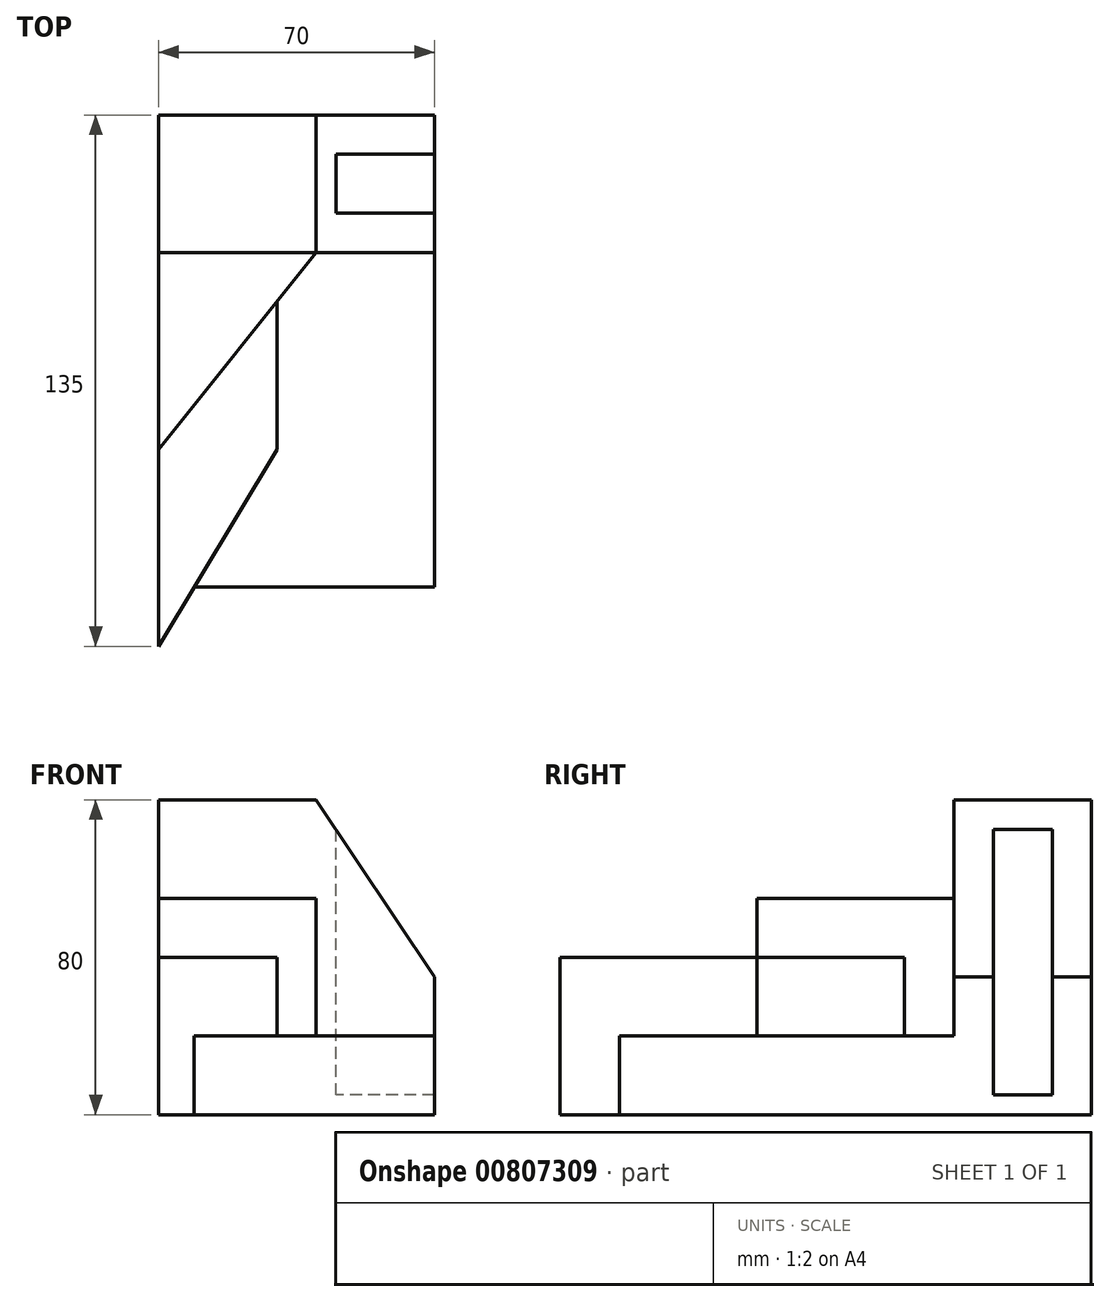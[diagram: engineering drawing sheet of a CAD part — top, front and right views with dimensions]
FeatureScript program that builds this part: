
annotation { "Feature Type Name" : "Feature", "Feature Type Description" : "" }
export const myFeature = defineFeature(function(context is Context, id is Id, definition is map)
    precondition{}
    {
        {
            var Q0;
            Q0=qCreatedBy(makeId("Top.planeOp"),FACE);
            var sketch = newSketch(context, id + "F0", { "sketchPlane" : qUnion([Q0])});
            skLineSegment(sketch, "E0.bottom", {"start": v(0, 0) * mm, "end": v(70, 0) * mm});
            skLineSegment(sketch, "E0.top", {"start": v(0, 135) * mm, "end": v(70, 135) * mm});
            skLineSegment(sketch, "E0.left", {"start": v(0, 0) * mm, "end": v(0, 135) * mm});
            skLineSegment(sketch, "E0.right", {"start": v(70, 0) * mm, "end": v(70, 135) * mm});
            skLineSegment(sketch, "E1", {"start": v(0, 100) * mm, "end": v(70, 100) * mm});
            skLineSegment(sketch, "E2", {"start": v(0, 50) * mm, "end": v(40, 100) * mm});
            skLineSegment(sketch, "E3", {"start": v(0, 0) * mm, "end": v(30, 50) * mm});
            skLineSegment(sketch, "E4", {"start": v(30, 50) * mm, "end": v(30, 87.5) * mm});
            skLineSegment(sketch, "E5", {"start": v(9, 15) * mm, "end": v(70, 15) * mm});
            skSolve(sketch);
        }
        {
            var Q0;
            {var subQ0=sQuery(id+"F0.wireOp",EDGE,"E4");Q0=makeQuery(id+"F0.imprint","IMPRINT",FACE,{"disambiguationData":[TD([[makeQuery(id+"F0.imprint","IMPRINT",EDGE,{"derivedFrom":subQ0}),1.0]])]});}
            extrude(context, id + "F1", {"entities" : qUnion([Q0]), "depth" : 40 * mm, "offsetDistance" : 25 * mm});
        }
        {
            var Q0;
            {var subQ0=sQuery(id+"F0.wireOp",EDGE,"E1");var subQ1=sQuery(id+"F0.wireOp",EDGE,"E0.left");var subQ2=makeQuery(id+"F0.imprint","INTERSECT",VERTEX,{"derivedFrom":[subQ1,subQ0]});Q0=makeQuery(id+"F0.imprint","IMPRINT",FACE,{"disambiguationData":[TD([[makeQuery(id+"F0.imprint","IMPRINT",EDGE,{"disambiguationData":[TD([[subQ2,1.0]])],"derivedFrom":subQ1}),-1.0]])]});}
            extrude(context, id + "F2", {"entities" : qUnion([Q0]), "operationType" : NewBodyOperationType.ADD, "depth" : 55 * mm, "offsetDistance" : 25 * mm});
        }
        {
            var Q0;
            {var subQ5=sQuery(id+"F0.wireOp",EDGE,"E0.top");Q0=makeQuery(id+"F0.imprint","IMPRINT",FACE,{"disambiguationData":[TD([[makeQuery(id+"F0.imprint","IMPRINT",EDGE,{"derivedFrom":subQ5}),-1.0]])]});}
            extrude(context, id + "F3", {"entities" : qUnion([Q0]), "operationType" : NewBodyOperationType.ADD, "depth" : 80 * mm, "offsetDistance" : 25 * mm});
        }
        {
            var Q0;
            {var subQ0=sQuery(id+"F0.wireOp",EDGE,"E4");Q0=makeQuery(id+"F0.imprint","IMPRINT",FACE,{"disambiguationData":[TD([[makeQuery(id+"F0.imprint","IMPRINT",EDGE,{"derivedFrom":subQ0}),-1.0]])]});}
            extrude(context, id + "F4", {"entities" : qUnion([Q0]), "operationType" : NewBodyOperationType.ADD, "depth" : 20 * mm, "offsetDistance" : 25 * mm});
        }
        {
            var Q0;
            Q0=makeQuery(id+"F3.opExtrude","CAP_FACE",FACE,{"disambiguationData":[OSD([sQuery(id+"F0.wireOp",EDGE,"E0.top"),sQuery(id+"F0.wireOp",EDGE,"E0.left"),sQuery(id+"F0.wireOp",EDGE,"E0.right"),sQuery(id+"F0.wireOp",EDGE,"E1")])],"isStart":false});
            var sketch = newSketch(context, id + "F5", { "sketchPlane" : qUnion([Q0])});
            skLineSegment(sketch, "E6.0", {"start": v(0, 100) * mm, "end": v(0, 135) * mm});
            skLineSegment(sketch, "E7.0", {"start": v(70, 15) * mm, "end": v(70, 135) * mm});
            skLineSegment(sketch, "E8.0", {"start": v(0, 135) * mm, "end": v(70, 135) * mm});
            skLineSegment(sketch, "E9", {"start": v(0, 100) * mm, "end": v(70, 100) * mm});
            skLineSegment(sketch, "E10", {"start": v(40, 100) * mm, "end": v(40, 135) * mm});
            skLineSegment(sketch, "E11", {"start": v(70, 110) * mm, "end": v(45, 110) * mm});
            skLineSegment(sketch, "E12", {"start": v(45, 110) * mm, "end": v(45, 125) * mm});
            skLineSegment(sketch, "E13", {"start": v(45, 125) * mm, "end": v(70, 125) * mm});
            skSolve(sketch);
        }
        {
            var Q0;
            {var subQ0=sQuery(id+"F5.wireOp",EDGE,"E11");Q0=makeQuery(id+"F5.imprint","IMPRINT",FACE,{"disambiguationData":[TD([[makeQuery(id+"F5.imprint","IMPRINT",EDGE,{"derivedFrom":subQ0}),-1.0]])]});}
            extrude(context, id + "F6", {"entities" : qUnion([Q0]), "operationType" : NewBodyOperationType.REMOVE, "oppositeDirection" : true, "depth" : 75 * mm, "offsetDistance" : 25 * mm});
        }
        {
            var Q0;
            Q0=makeQuery(id+"F3.opExtrude","SWEPT_FACE",FACE,{"disambiguationData":[OSD([sQuery(id+"F0.wireOp",EDGE,"E0.top")])]});
            var sketch = newSketch(context, id + "F7", { "sketchPlane" : qUnion([Q0])});
            skLineSegment(sketch, "E14.0.0", {"start": v(-70, 0) * mm, "end": v(0, 0) * mm});
            skLineSegment(sketch, "E14.0.1", {"start": v(0, 0) * mm, "end": v(0, 80) * mm});
            skLineSegment(sketch, "E14.0.2", {"start": v(0, 80) * mm, "end": v(-70, 80) * mm});
            skLineSegment(sketch, "E14.0.3", {"start": v(-70, 80) * mm, "end": v(-70, 0) * mm});
            skLineSegment(sketch, "E15", {"start": v(-70, 35) * mm, "end": v(-40, 80) * mm});
            skSolve(sketch);
        }
        {
            var Q0;
            {var subQ3=sQuery(id+"F7.wireOp",EDGE,"E15");Q0=makeQuery(id+"F7.imprint","IMPRINT",FACE,{"disambiguationData":[TD([[makeQuery(id+"F7.imprint","IMPRINT",EDGE,{"derivedFrom":subQ3}),1.0]])]});}
            var Q1;
            Q1=makeQuery(id+"F3.opExtrude","SWEPT_FACE",FACE,{"disambiguationData":[OSD([sQuery(id+"F0.wireOp",EDGE,"E1")])]});
            extrude(context, id + "F8", {"entities" : qUnion([Q0]), "operationType" : NewBodyOperationType.REMOVE, "endBound" : BoundingType.UP_TO_SURFACE, "oppositeDirection" : true, "depth" : 25 * mm, "endBoundEntityFace" : qUnion([Q1]), "offsetDistance" : 25 * mm});
        }
    });
